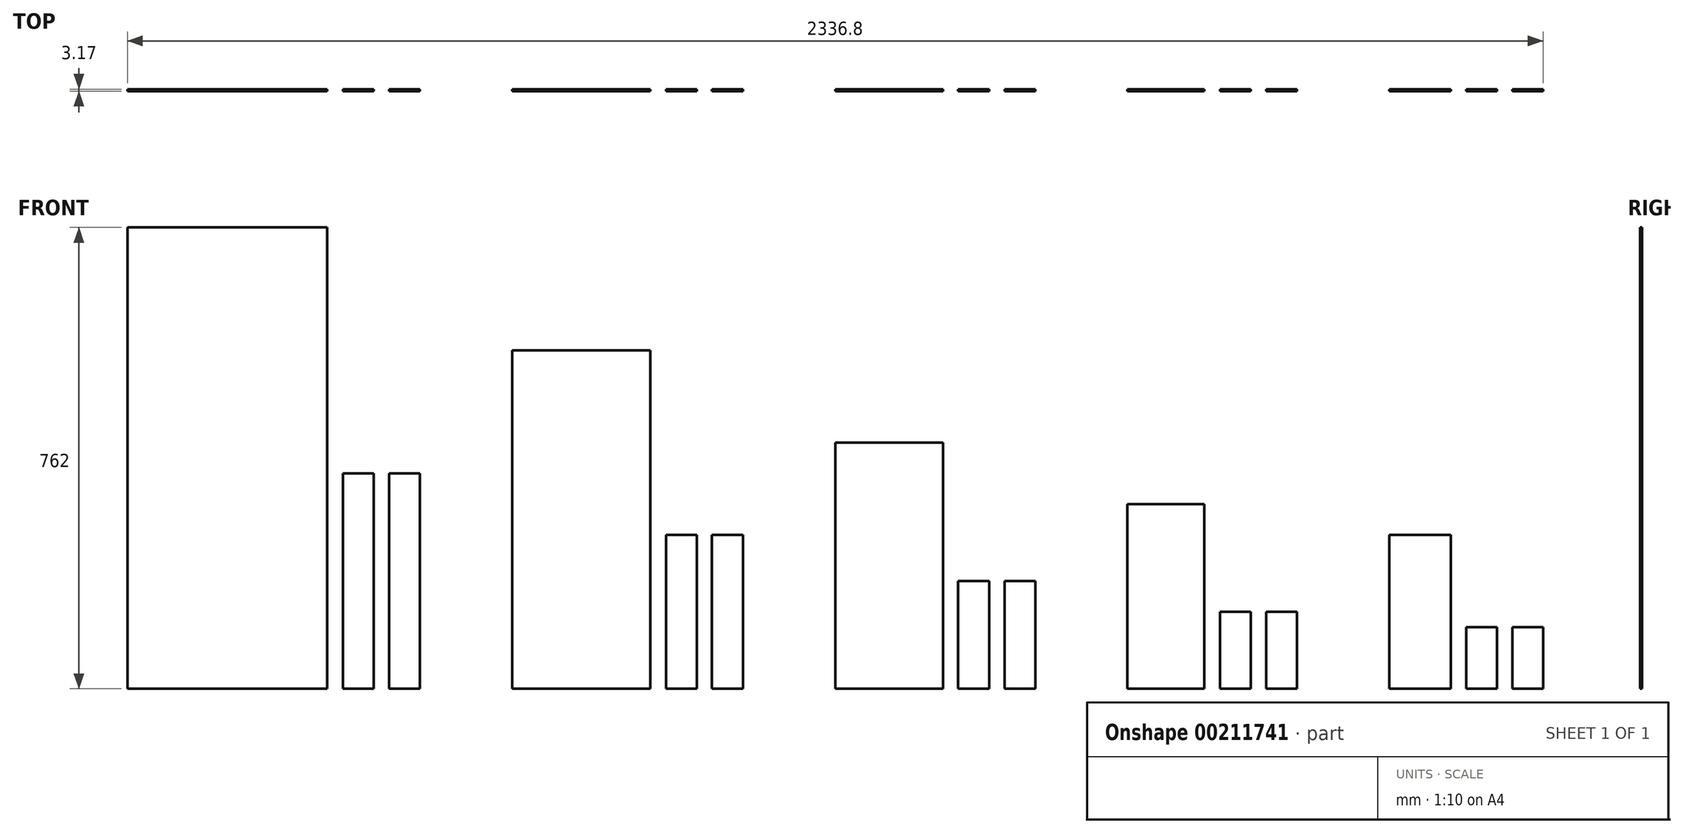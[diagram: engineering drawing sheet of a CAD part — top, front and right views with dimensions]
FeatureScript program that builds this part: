
annotation { "Feature Type Name" : "Feature", "Feature Type Description" : "" }
export const myFeature = defineFeature(function(context is Context, id is Id, definition is map)
    precondition{}
    {
        {
            var Q0;
            Q0=qCreatedBy(makeId("Front.planeOp"),FACE);
            var sketch = newSketch(context, id + "F0", { "sketchPlane" : qUnion([Q0])});
            skLineSegment(sketch, "E0.bottom", {"start": v(-330.2, 762) * mm, "end": v(0, 762) * mm});
            skLineSegment(sketch, "E0.top", {"start": v(-330.2, 0) * mm, "end": v(0, 0) * mm});
            skLineSegment(sketch, "E0.left", {"start": v(-330.2, 762) * mm, "end": v(-330.2, 0) * mm});
            skLineSegment(sketch, "E0.right", {"start": v(0, 762) * mm, "end": v(0, 0) * mm});
            skLineSegment(sketch, "E1", {"start": v(-330.2, 406.4) * mm, "end": v(0, 406.4) * mm, "construction": true});
            skLineSegment(sketch, "E2", {"start": v(0, 355.6) * mm, "end": v(-330.2, 355.6) * mm, "construction": true});
            skLineSegment(sketch, "E3.bottom", {"start": v(25.4, 355.6) * mm, "end": v(76.2, 355.6) * mm});
            skLineSegment(sketch, "E3.top", {"start": v(25.4, 0) * mm, "end": v(76.2, 0) * mm});
            skLineSegment(sketch, "E3.left", {"start": v(25.4, 355.6) * mm, "end": v(25.4, 0) * mm});
            skLineSegment(sketch, "E3.right", {"start": v(76.2, 355.6) * mm, "end": v(76.2, 0) * mm});
            skLineSegment(sketch, "E4.bottom", {"start": v(101.6, 355.6) * mm, "end": v(152.4, 355.6) * mm});
            skLineSegment(sketch, "E4.top", {"start": v(101.6, 0) * mm, "end": v(152.4, 0) * mm});
            skLineSegment(sketch, "E4.left", {"start": v(101.6, 355.6) * mm, "end": v(101.6, 0) * mm});
            skLineSegment(sketch, "E4.right", {"start": v(152.4, 355.6) * mm, "end": v(152.4, 0) * mm});
            skLineSegment(sketch, "E5", {"start": v(-330.2, 406.4) * mm, "end": v(-330.2, 355.6) * mm, "construction": true});
            skSolve(sketch);
        }
        {
            var Q0;
            Q0=qCreatedBy(makeId("Front.planeOp"),FACE);
            var sketch = newSketch(context, id + "F1", { "sketchPlane" : qUnion([Q0])});
            skLineSegment(sketch, "E6.bottom", {"start": v(304.8, 558.8) * mm, "end": v(533.4, 558.8) * mm});
            skLineSegment(sketch, "E6.top", {"start": v(304.8, 0) * mm, "end": v(533.4, 0) * mm});
            skLineSegment(sketch, "E6.left", {"start": v(304.8, 558.8) * mm, "end": v(304.8, 0) * mm});
            skLineSegment(sketch, "E6.right", {"start": v(533.4, 558.8) * mm, "end": v(533.4, 0) * mm});
            skLineSegment(sketch, "E7", {"start": v(304.8, 304.8) * mm, "end": v(533.4, 304.8) * mm, "construction": true});
            skLineSegment(sketch, "E8", {"start": v(533.4, 254) * mm, "end": v(304.8, 254) * mm, "construction": true});
            skLineSegment(sketch, "E9.bottom", {"start": v(558.8, 254) * mm, "end": v(609.6, 254) * mm});
            skLineSegment(sketch, "E9.top", {"start": v(558.8, 0) * mm, "end": v(609.6, 0) * mm});
            skLineSegment(sketch, "E9.left", {"start": v(558.8, 254) * mm, "end": v(558.8, 0) * mm});
            skLineSegment(sketch, "E9.right", {"start": v(609.6, 254) * mm, "end": v(609.6, 0) * mm});
            skLineSegment(sketch, "E10.bottom", {"start": v(635, 254) * mm, "end": v(685.8, 254) * mm});
            skLineSegment(sketch, "E10.top", {"start": v(635, 0) * mm, "end": v(685.8, 0) * mm});
            skLineSegment(sketch, "E10.left", {"start": v(635, 254) * mm, "end": v(635, 0) * mm});
            skLineSegment(sketch, "E10.right", {"start": v(685.8, 254) * mm, "end": v(685.8, 0) * mm});
            skLineSegment(sketch, "E11", {"start": v(304.8, 304.8) * mm, "end": v(304.8, 254) * mm, "construction": true});
            skSolve(sketch);
        }
        {
            var Q0;
            Q0=qCreatedBy(makeId("Front.planeOp"),FACE);
            var sketch = newSketch(context, id + "F2", { "sketchPlane" : qUnion([Q0])});
            skLineSegment(sketch, "E12.bottom", {"start": v(838.2, 406.4) * mm, "end": v(1016, 406.4) * mm});
            skLineSegment(sketch, "E12.top", {"start": v(838.2, 0) * mm, "end": v(1016, 0) * mm});
            skLineSegment(sketch, "E12.left", {"start": v(838.2, 406.4) * mm, "end": v(838.2, 0) * mm});
            skLineSegment(sketch, "E12.right", {"start": v(1016, 406.4) * mm, "end": v(1016, 0) * mm});
            skLineSegment(sketch, "E13", {"start": v(838.2, 228.6) * mm, "end": v(1016, 228.6) * mm, "construction": true});
            skLineSegment(sketch, "E14", {"start": v(1016, 177.8) * mm, "end": v(838.2, 177.8) * mm, "construction": true});
            skLineSegment(sketch, "E15.bottom", {"start": v(1041.4, 177.8) * mm, "end": v(1092.2, 177.8) * mm});
            skLineSegment(sketch, "E15.top", {"start": v(1041.4, 0) * mm, "end": v(1092.2, 0) * mm});
            skLineSegment(sketch, "E15.left", {"start": v(1041.4, 177.8) * mm, "end": v(1041.4, 0) * mm});
            skLineSegment(sketch, "E15.right", {"start": v(1092.2, 177.8) * mm, "end": v(1092.2, 0) * mm});
            skLineSegment(sketch, "E16.bottom", {"start": v(1117.6, 177.8) * mm, "end": v(1168.4, 177.8) * mm});
            skLineSegment(sketch, "E16.top", {"start": v(1117.6, 0) * mm, "end": v(1168.4, 0) * mm});
            skLineSegment(sketch, "E16.left", {"start": v(1117.6, 177.8) * mm, "end": v(1117.6, 0) * mm});
            skLineSegment(sketch, "E16.right", {"start": v(1168.4, 177.8) * mm, "end": v(1168.4, 0) * mm});
            skLineSegment(sketch, "E17", {"start": v(838.2, 228.6) * mm, "end": v(838.2, 177.8) * mm, "construction": true});
            skSolve(sketch);
        }
        {
            var Q0;
            Q0=qCreatedBy(makeId("Front.planeOp"),FACE);
            var sketch = newSketch(context, id + "F3", { "sketchPlane" : qUnion([Q0])});
            skLineSegment(sketch, "E18.bottom", {"start": v(1320.8, 304.8) * mm, "end": v(1447.8, 304.8) * mm});
            skLineSegment(sketch, "E18.top", {"start": v(1320.8, 0) * mm, "end": v(1447.8, 0) * mm});
            skLineSegment(sketch, "E18.left", {"start": v(1320.8, 304.8) * mm, "end": v(1320.8, 0) * mm});
            skLineSegment(sketch, "E18.right", {"start": v(1447.8, 304.8) * mm, "end": v(1447.8, 0) * mm});
            skLineSegment(sketch, "E19", {"start": v(1320.8, 177.8) * mm, "end": v(1447.8, 177.8) * mm, "construction": true});
            skLineSegment(sketch, "E20", {"start": v(1447.8, 127) * mm, "end": v(1320.8, 127) * mm, "construction": true});
            skLineSegment(sketch, "E21.bottom", {"start": v(1473.2, 127) * mm, "end": v(1524, 127) * mm});
            skLineSegment(sketch, "E21.top", {"start": v(1473.2, 0) * mm, "end": v(1524, 0) * mm});
            skLineSegment(sketch, "E21.left", {"start": v(1473.2, 127) * mm, "end": v(1473.2, 0) * mm});
            skLineSegment(sketch, "E21.right", {"start": v(1524, 127) * mm, "end": v(1524, 0) * mm});
            skLineSegment(sketch, "E22.bottom", {"start": v(1549.4, 127) * mm, "end": v(1600.2, 127) * mm});
            skLineSegment(sketch, "E22.top", {"start": v(1549.4, 0) * mm, "end": v(1600.2, 0) * mm});
            skLineSegment(sketch, "E22.left", {"start": v(1549.4, 127) * mm, "end": v(1549.4, 0) * mm});
            skLineSegment(sketch, "E22.right", {"start": v(1600.2, 127) * mm, "end": v(1600.2, 0) * mm});
            skLineSegment(sketch, "E23", {"start": v(1320.8, 177.8) * mm, "end": v(1320.8, 127) * mm, "construction": true});
            skSolve(sketch);
        }
        {
            var Q0;
            Q0=qCreatedBy(makeId("Front.planeOp"),FACE);
            var sketch = newSketch(context, id + "F4", { "sketchPlane" : qUnion([Q0])});
            skLineSegment(sketch, "E24.bottom", {"start": v(1752.6, 254) * mm, "end": v(1854.2, 254) * mm});
            skLineSegment(sketch, "E24.top", {"start": v(1752.6, 0) * mm, "end": v(1854.2, 0) * mm});
            skLineSegment(sketch, "E24.left", {"start": v(1752.6, 254) * mm, "end": v(1752.6, 0) * mm});
            skLineSegment(sketch, "E24.right", {"start": v(1854.2, 254) * mm, "end": v(1854.2, 0) * mm});
            skLineSegment(sketch, "E25", {"start": v(1752.6, 152.4) * mm, "end": v(1854.2, 152.4) * mm, "construction": true});
            skLineSegment(sketch, "E26", {"start": v(1854.2, 101.6) * mm, "end": v(1752.6, 101.6) * mm, "construction": true});
            skLineSegment(sketch, "E27.bottom", {"start": v(1879.6, 101.6) * mm, "end": v(1930.4, 101.6) * mm});
            skLineSegment(sketch, "E27.top", {"start": v(1879.6, 0) * mm, "end": v(1930.4, 0) * mm});
            skLineSegment(sketch, "E27.left", {"start": v(1879.6, 101.6) * mm, "end": v(1879.6, 0) * mm});
            skLineSegment(sketch, "E27.right", {"start": v(1930.4, 101.6) * mm, "end": v(1930.4, 0) * mm});
            skLineSegment(sketch, "E28.bottom", {"start": v(1955.8, 101.6) * mm, "end": v(2006.6, 101.6) * mm});
            skLineSegment(sketch, "E28.top", {"start": v(1955.8, 0) * mm, "end": v(2006.6, 0) * mm});
            skLineSegment(sketch, "E28.left", {"start": v(1955.8, 101.6) * mm, "end": v(1955.8, 0) * mm});
            skLineSegment(sketch, "E28.right", {"start": v(2006.6, 101.6) * mm, "end": v(2006.6, 0) * mm});
            skLineSegment(sketch, "E29", {"start": v(1752.6, 152.4) * mm, "end": v(1752.6, 101.6) * mm, "construction": true});
            skSolve(sketch);
        }
        {
            var Q0;
            Q0=makeQuery(id+"F0.imprint","IMPRINT",FACE,{"disambiguationData":[TD([[makeQuery(id+"F0.imprint","IMPRINT",EDGE,{"derivedFrom":sQuery(id+"F0.wireOp",EDGE,"E0.bottom")}),-1.0]])]});
            var Q1;
            Q1=makeQuery(id+"F0.imprint","IMPRINT",FACE,{"disambiguationData":[TD([[makeQuery(id+"F0.imprint","IMPRINT",EDGE,{"derivedFrom":sQuery(id+"F0.wireOp",EDGE,"E3.bottom")}),-1.0]])]});
            var Q2;
            Q2=makeQuery(id+"F0.imprint","IMPRINT",FACE,{"disambiguationData":[TD([[makeQuery(id+"F0.imprint","IMPRINT",EDGE,{"derivedFrom":sQuery(id+"F0.wireOp",EDGE,"E4.bottom")}),-1.0]])]});
            var Q3;
            Q3=makeQuery(id+"F1.imprint","IMPRINT",FACE,{"disambiguationData":[TD([[makeQuery(id+"F1.imprint","IMPRINT",EDGE,{"derivedFrom":sQuery(id+"F1.wireOp",EDGE,"E6.bottom")}),-1.0]])]});
            var Q4;
            Q4=makeQuery(id+"F1.imprint","IMPRINT",FACE,{"disambiguationData":[TD([[makeQuery(id+"F1.imprint","IMPRINT",EDGE,{"derivedFrom":sQuery(id+"F1.wireOp",EDGE,"E9.bottom")}),-1.0]])]});
            var Q5;
            Q5=makeQuery(id+"F1.imprint","IMPRINT",FACE,{"disambiguationData":[TD([[makeQuery(id+"F1.imprint","IMPRINT",EDGE,{"derivedFrom":sQuery(id+"F1.wireOp",EDGE,"E10.bottom")}),-1.0]])]});
            var Q6;
            Q6=makeQuery(id+"F2.imprint","IMPRINT",FACE,{"disambiguationData":[TD([[makeQuery(id+"F2.imprint","IMPRINT",EDGE,{"derivedFrom":sQuery(id+"F2.wireOp",EDGE,"E12.bottom")}),-1.0]])]});
            var Q7;
            Q7=makeQuery(id+"F2.imprint","IMPRINT",FACE,{"disambiguationData":[TD([[makeQuery(id+"F2.imprint","IMPRINT",EDGE,{"derivedFrom":sQuery(id+"F2.wireOp",EDGE,"E15.bottom")}),-1.0]])]});
            var Q8;
            Q8=makeQuery(id+"F2.imprint","IMPRINT",FACE,{"disambiguationData":[TD([[makeQuery(id+"F2.imprint","IMPRINT",EDGE,{"derivedFrom":sQuery(id+"F2.wireOp",EDGE,"E16.bottom")}),-1.0]])]});
            var Q9;
            Q9=makeQuery(id+"F3.imprint","IMPRINT",FACE,{"disambiguationData":[TD([[makeQuery(id+"F3.imprint","IMPRINT",EDGE,{"derivedFrom":sQuery(id+"F3.wireOp",EDGE,"E22.bottom")}),-1.0]])]});
            var Q10;
            Q10=makeQuery(id+"F3.imprint","IMPRINT",FACE,{"disambiguationData":[TD([[makeQuery(id+"F3.imprint","IMPRINT",EDGE,{"derivedFrom":sQuery(id+"F3.wireOp",EDGE,"E21.bottom")}),-1.0]])]});
            var Q11;
            Q11=makeQuery(id+"F3.imprint","IMPRINT",FACE,{"disambiguationData":[TD([[makeQuery(id+"F3.imprint","IMPRINT",EDGE,{"derivedFrom":sQuery(id+"F3.wireOp",EDGE,"E18.bottom")}),-1.0]])]});
            var Q12;
            Q12=makeQuery(id+"F4.imprint","IMPRINT",FACE,{"disambiguationData":[TD([[makeQuery(id+"F4.imprint","IMPRINT",EDGE,{"derivedFrom":sQuery(id+"F4.wireOp",EDGE,"E28.bottom")}),-1.0]])]});
            var Q13;
            Q13=makeQuery(id+"F4.imprint","IMPRINT",FACE,{"disambiguationData":[TD([[makeQuery(id+"F4.imprint","IMPRINT",EDGE,{"derivedFrom":sQuery(id+"F4.wireOp",EDGE,"E27.bottom")}),-1.0]])]});
            var Q14;
            Q14=makeQuery(id+"F4.imprint","IMPRINT",FACE,{"disambiguationData":[TD([[makeQuery(id+"F4.imprint","IMPRINT",EDGE,{"derivedFrom":sQuery(id+"F4.wireOp",EDGE,"E24.bottom")}),-1.0]])]});
            extrude(context, id + "F5", {"entities" : qUnion([Q0, Q1, Q2, Q3, Q4, Q5, Q6, Q7, Q8, Q9, Q10, Q11, Q12, Q13, Q14]), "depth" : 3.17 * mm});
        }
    });
